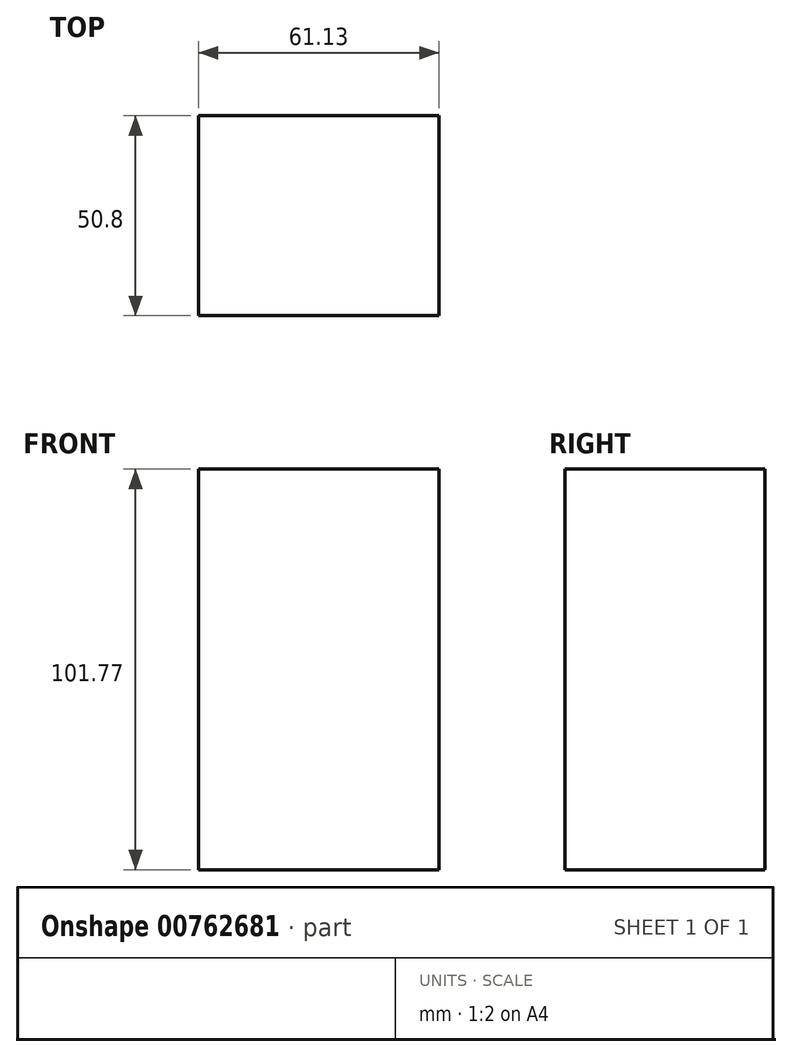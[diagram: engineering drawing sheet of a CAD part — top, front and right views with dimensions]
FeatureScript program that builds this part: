
annotation { "Feature Type Name" : "Feature", "Feature Type Description" : "" }
export const myFeature = defineFeature(function(context is Context, id is Id, definition is map)
    precondition{}
    {
        {
            var Q0;
            Q0=qCreatedBy(makeId("Front.planeOp"),FACE);
            var sketch = newSketch(context, id + "F0", { "sketchPlane" : qUnion([Q0])});
            skLineSegment(sketch, "E0.bottom", {"start": v(-15.86, 28.99) * mm, "end": v(45.27, 28.99) * mm});
            skLineSegment(sketch, "E0.top", {"start": v(-15.86, -72.78) * mm, "end": v(45.27, -72.78) * mm});
            skLineSegment(sketch, "E0.left", {"start": v(-15.86, 28.99) * mm, "end": v(-15.86, -72.78) * mm});
            skLineSegment(sketch, "E0.right", {"start": v(45.27, 28.99) * mm, "end": v(45.27, -72.78) * mm});
            skSolve(sketch);
        }
        {
            var Q0;
            Q0 = qSketchRegion(id + "F0", true);
            extrude(context, id + "F1", {"entities" : qUnion([Q0]), "depth" : 50.8 * mm, "offsetDistance" : 25.4 * mm});
        }
    });
